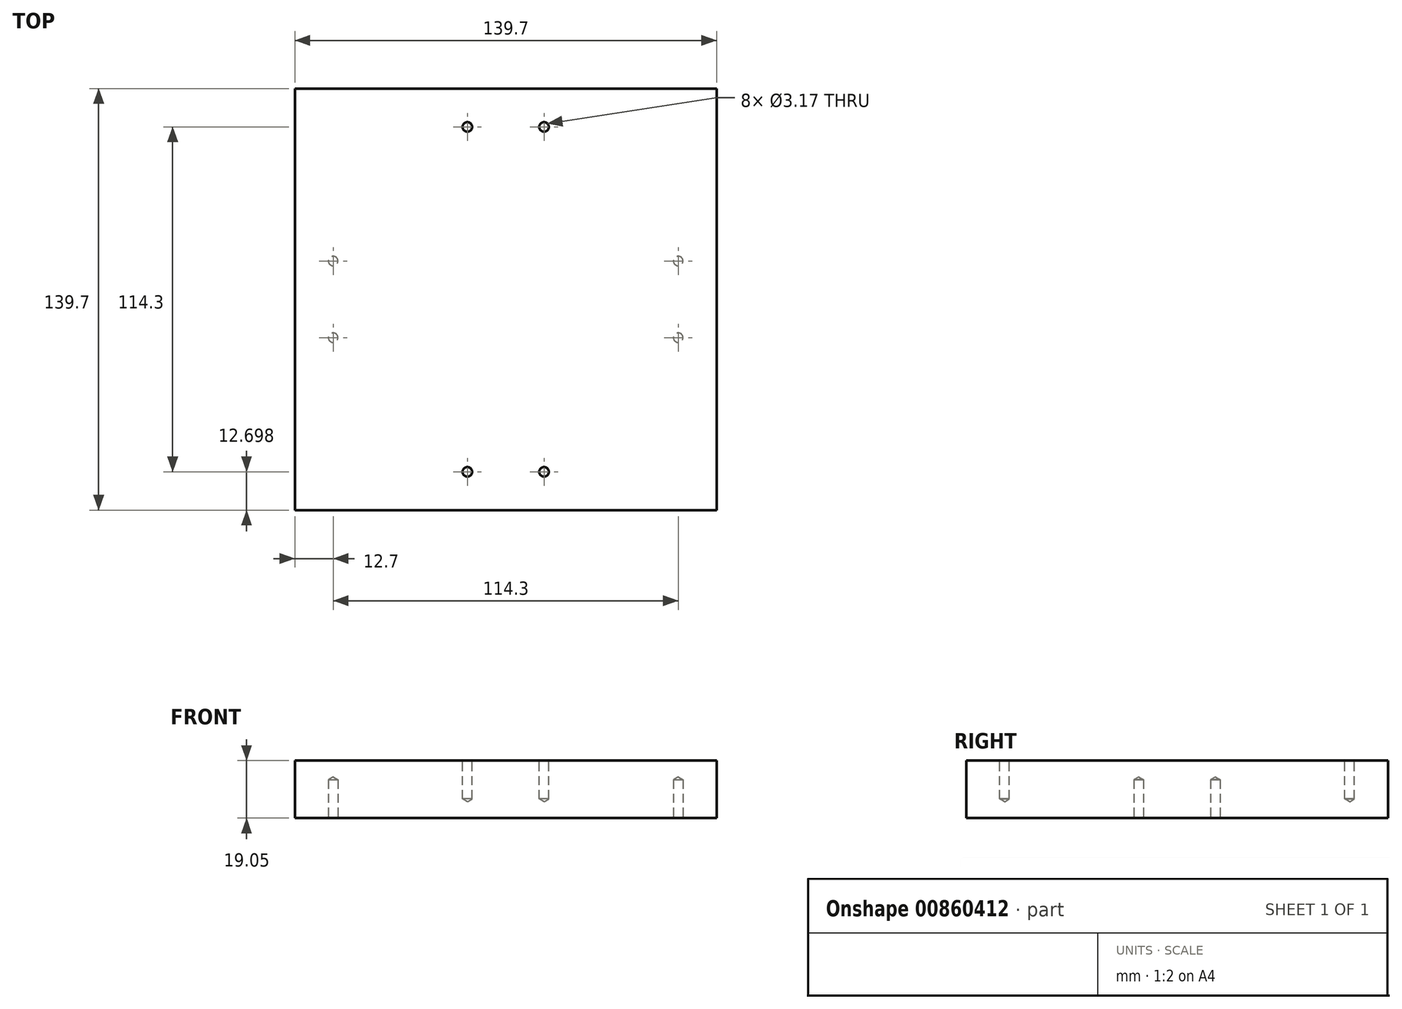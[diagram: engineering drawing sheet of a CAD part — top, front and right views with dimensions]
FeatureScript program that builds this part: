
annotation { "Feature Type Name" : "Feature", "Feature Type Description" : "" }
export const myFeature = defineFeature(function(context is Context, id is Id, definition is map)
    precondition{}
    {
        {
            var Q0;
            Q0=qCreatedBy(makeId("Top.planeOp"),FACE);
            var sketch = newSketch(context, id + "F0", { "sketchPlane" : qUnion([Q0])});
            skLineSegment(sketch, "E0.bottom", {"start": v(-143.3, 83.42) * mm, "end": v(-3.6, 83.42) * mm});
            skLineSegment(sketch, "E0.top", {"start": v(-143.3, -56.28) * mm, "end": v(-3.6, -56.28) * mm});
            skLineSegment(sketch, "E0.left", {"start": v(-143.3, 83.42) * mm, "end": v(-143.3, -56.28) * mm});
            skLineSegment(sketch, "E0.right", {"start": v(-3.6, 83.42) * mm, "end": v(-3.6, -56.28) * mm});
            skSolve(sketch);
        }
        {
            var Q0;
            Q0=makeQuery(id+"F0.imprint","IMPRINT",FACE,{"disambiguationData":[TD([[makeQuery(id+"F0.imprint","IMPRINT",EDGE,{"derivedFrom":sQuery(id+"F0.wireOp",EDGE,"E0.bottom")}),-1.0]])]});
            extrude(context, id + "F1", {"entities" : qUnion([Q0]), "depth" : 19.05 * mm, "offsetDistance" : 25.4 * mm});
        }
        {
            var Q0;
            Q0=makeQuery(id+"F1.opExtrude","CAP_FACE",FACE,{"disambiguationData":[OSD([sQuery(id+"F0.wireOp",EDGE,"E0.bottom"),sQuery(id+"F0.wireOp",EDGE,"E0.top"),sQuery(id+"F0.wireOp",EDGE,"E0.left"),sQuery(id+"F0.wireOp",EDGE,"E0.right")])],"isStart":false});
            var sketch = newSketch(context, id + "F2", { "sketchPlane" : qUnion([Q0])});
            skPoint(sketch, "E1", {"position": v(-86.16, 70.72) * mm});
            skPoint(sketch, "E2", {"position": v(-60.76, 70.72) * mm});
            skPoint(sketch, "E3", {"position": v(-86.16, -43.58) * mm});
            skPoint(sketch, "E4", {"position": v(-60.76, -43.58) * mm});
            skSolve(sketch);
        }
        {
            var Q0;
            Q0=sQuery(id+"F2.wireOp",VERTEX,"E1");
            var Q1;
            Q1=sQuery(id+"F2.wireOp",VERTEX,"E2");
            var Q2;
            Q2=sQuery(id+"F2.wireOp",VERTEX,"E4");
            var Q3;
            Q3=sQuery(id+"F2.wireOp",VERTEX,"E3");
            var Q4;
            Q4=makeQuery(id+"F1.opExtrude","SWEPT_BODY",BODY,{"disambiguationData":[OSD([sQuery(id+"F0.wireOp",EDGE,"E0.bottom"),sQuery(id+"F0.wireOp",EDGE,"E0.top"),sQuery(id+"F0.wireOp",EDGE,"E0.left"),sQuery(id+"F0.wireOp",EDGE,"E0.right")])]});
            hole(context, id + "F3", {"style" : HoleStyle.SIMPLE, "endStyle" : HoleEndStyle.BLIND, "holeDiameter" : 3.17 * mm, "majorDiameter" : 6.35 * mm, "holeDepth" : 12.7 * mm, "isTappedThrough" : true, "tappedDepth" : 12.7 * mm, "tapClearance" : 3, "locations" : qUnion([Q0, Q1, Q2, Q3]), "scope" : qUnion([Q4])});
        }
        {
            var Q0;
            Q0=makeQuery(id+"F1.opExtrude","CAP_FACE",FACE,{"disambiguationData":[OSD([sQuery(id+"F0.wireOp",EDGE,"E0.bottom"),sQuery(id+"F0.wireOp",EDGE,"E0.top"),sQuery(id+"F0.wireOp",EDGE,"E0.left"),sQuery(id+"F0.wireOp",EDGE,"E0.right")])],"isStart":true});
            var sketch = newSketch(context, id + "F4", { "sketchPlane" : qUnion([Q0])});
            skPoint(sketch, "E5", {"position": v(-130.6, -26.27) * mm});
            skPoint(sketch, "E6", {"position": v(-130.6, -0.87) * mm});
            skPoint(sketch, "E7", {"position": v(-16.3, -26.27) * mm});
            skPoint(sketch, "E8", {"position": v(-16.3, -0.87) * mm});
            skSolve(sketch);
        }
        {
            var Q0;
            Q0=sQuery(id+"F4.wireOp",VERTEX,"E5");
            var Q1;
            Q1=sQuery(id+"F4.wireOp",VERTEX,"E6");
            var Q2;
            Q2=sQuery(id+"F4.wireOp",VERTEX,"E7");
            var Q3;
            Q3=sQuery(id+"F4.wireOp",VERTEX,"E8");
            var Q4;
            Q4=makeQuery(id+"F1.opExtrude","SWEPT_BODY",BODY,{"disambiguationData":[OSD([sQuery(id+"F0.wireOp",EDGE,"E0.bottom"),sQuery(id+"F0.wireOp",EDGE,"E0.top"),sQuery(id+"F0.wireOp",EDGE,"E0.left"),sQuery(id+"F0.wireOp",EDGE,"E0.right")])]});
            hole(context, id + "F5", {"style" : HoleStyle.SIMPLE, "endStyle" : HoleEndStyle.BLIND, "holeDiameter" : 3.17 * mm, "majorDiameter" : 6.35 * mm, "holeDepth" : 12.7 * mm, "isTappedThrough" : true, "tappedDepth" : 12.7 * mm, "tapClearance" : 3, "locations" : qUnion([Q0, Q1, Q2, Q3]), "scope" : qUnion([Q4])});
        }
    });
